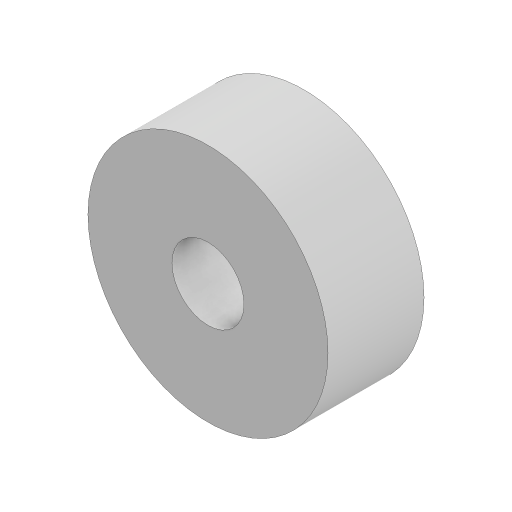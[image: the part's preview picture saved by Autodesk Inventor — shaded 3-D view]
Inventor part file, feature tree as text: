
AUTODESK INVENTOR PART (.ipt)
format: ipt  version: 2023.2 (Build 272271000, 271)  size: 96,768 bytes
history: native  units: mm
features: other x1, extrude x1, sketch x1
ambient origin geometry x8: Origin, YZ Plane, XZ Plane, XY Plane, X Axis, Y Axis, Z Axis, Center Point
bodies: Body1 (feature_tree)
feature tree (3):
  other  "솔리드1"
  extrude  "돌출1"  Depth=3.0mm
  sketch  "스케치1"
